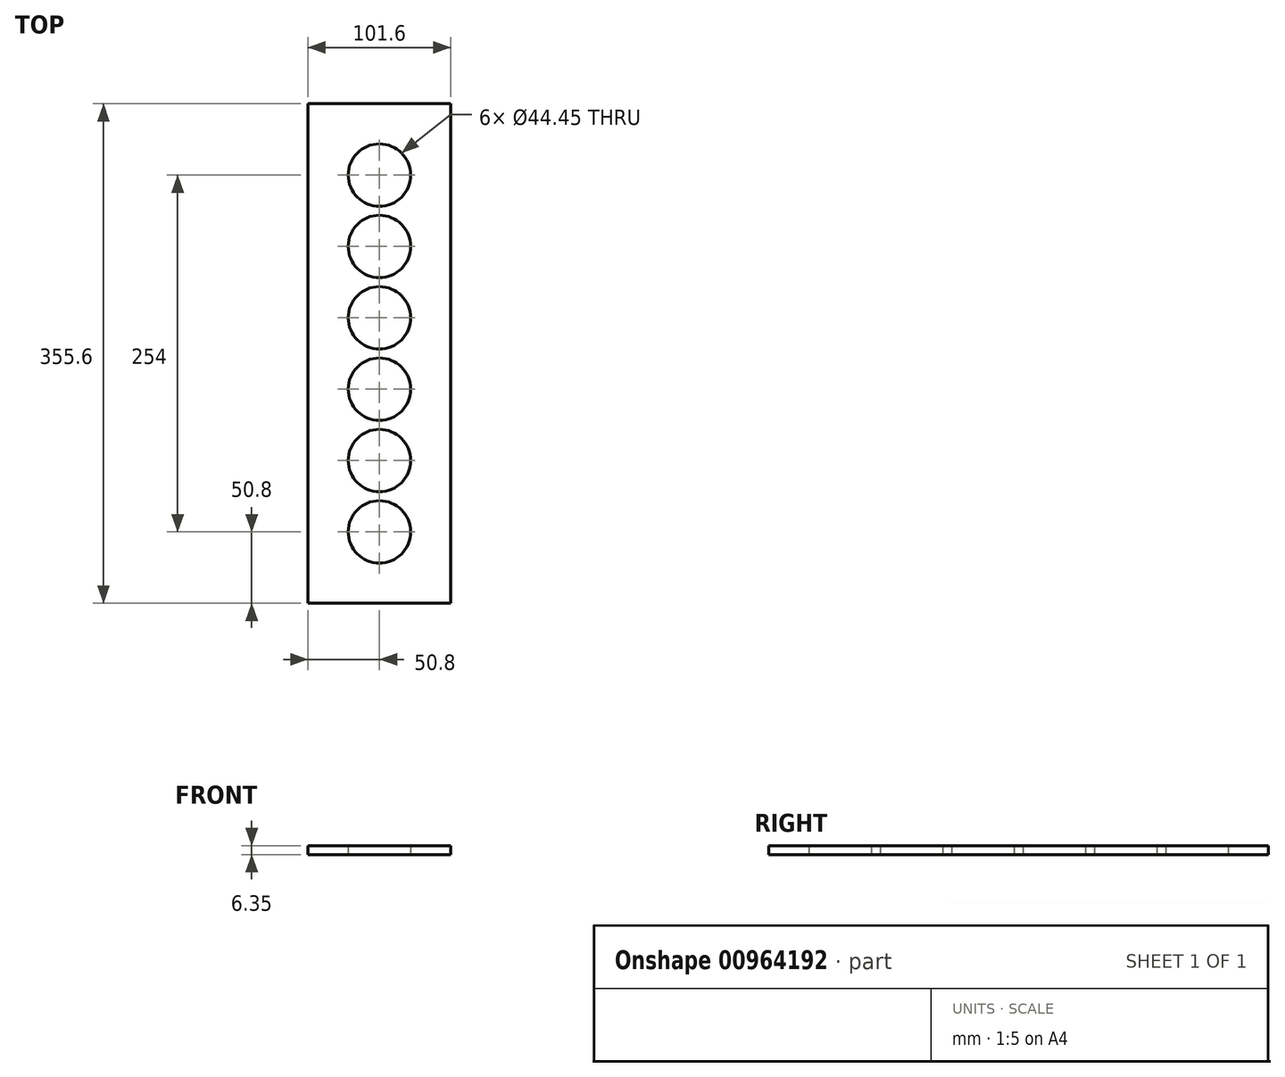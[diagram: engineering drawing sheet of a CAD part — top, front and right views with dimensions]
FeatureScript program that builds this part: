
annotation { "Feature Type Name" : "Feature", "Feature Type Description" : "" }
export const myFeature = defineFeature(function(context is Context, id is Id, definition is map)
    precondition{}
    {
        {
            var Q0;
            Q0=qCreatedBy(makeId("Top.planeOp"),FACE);
            var sketch = newSketch(context, id + "F0", { "sketchPlane" : qUnion([Q0])});
            skLineSegment(sketch, "E0.bottom", {"start": v(50.8, -177.8) * mm, "end": v(-50.8, -177.8) * mm});
            skLineSegment(sketch, "E0.top", {"start": v(50.8, 177.8) * mm, "end": v(-50.8, 177.8) * mm});
            skLineSegment(sketch, "E0.left", {"start": v(50.8, -177.8) * mm, "end": v(50.8, 177.8) * mm});
            skLineSegment(sketch, "E0.right", {"start": v(-50.8, -177.8) * mm, "end": v(-50.8, 177.8) * mm});
            skPoint(sketch, "E0.middle", {"position": v(0, 0) * mm});
            skPoint(sketch, "E1", {"position": v(0, 127) * mm});
            skPoint(sketch, "E2", {"position": v(0, 76.2) * mm});
            skPoint(sketch, "E3", {"position": v(0, 25.4) * mm});
            skPoint(sketch, "E4", {"position": v(0, -25.4) * mm});
            skPoint(sketch, "E5", {"position": v(0, -76.2) * mm});
            skPoint(sketch, "E6", {"position": v(0, -127) * mm});
            skCircle(sketch, "E7", {"center": v(0, -127) * mm, "radius": 22.23 * mm});
            skCircle(sketch, "E8", {"center": v(0, -76.2) * mm, "radius": 22.23 * mm});
            skCircle(sketch, "E9", {"center": v(0, -25.4) * mm, "radius": 22.23 * mm});
            skCircle(sketch, "E10", {"center": v(0, 25.4) * mm, "radius": 22.23 * mm});
            skCircle(sketch, "E11", {"center": v(0, 76.2) * mm, "radius": 22.23 * mm});
            skCircle(sketch, "E12", {"center": v(0, 127) * mm, "radius": 22.23 * mm});
            skSolve(sketch);
        }
        {
            var Q0;
            Q0 = qSketchRegion(id + "F0", true);
            extrude(context, id + "F1", {"entities" : qUnion([Q0]), "depth" : 6.35 * mm, "offsetDistance" : 25.4 * mm});
        }
    });
